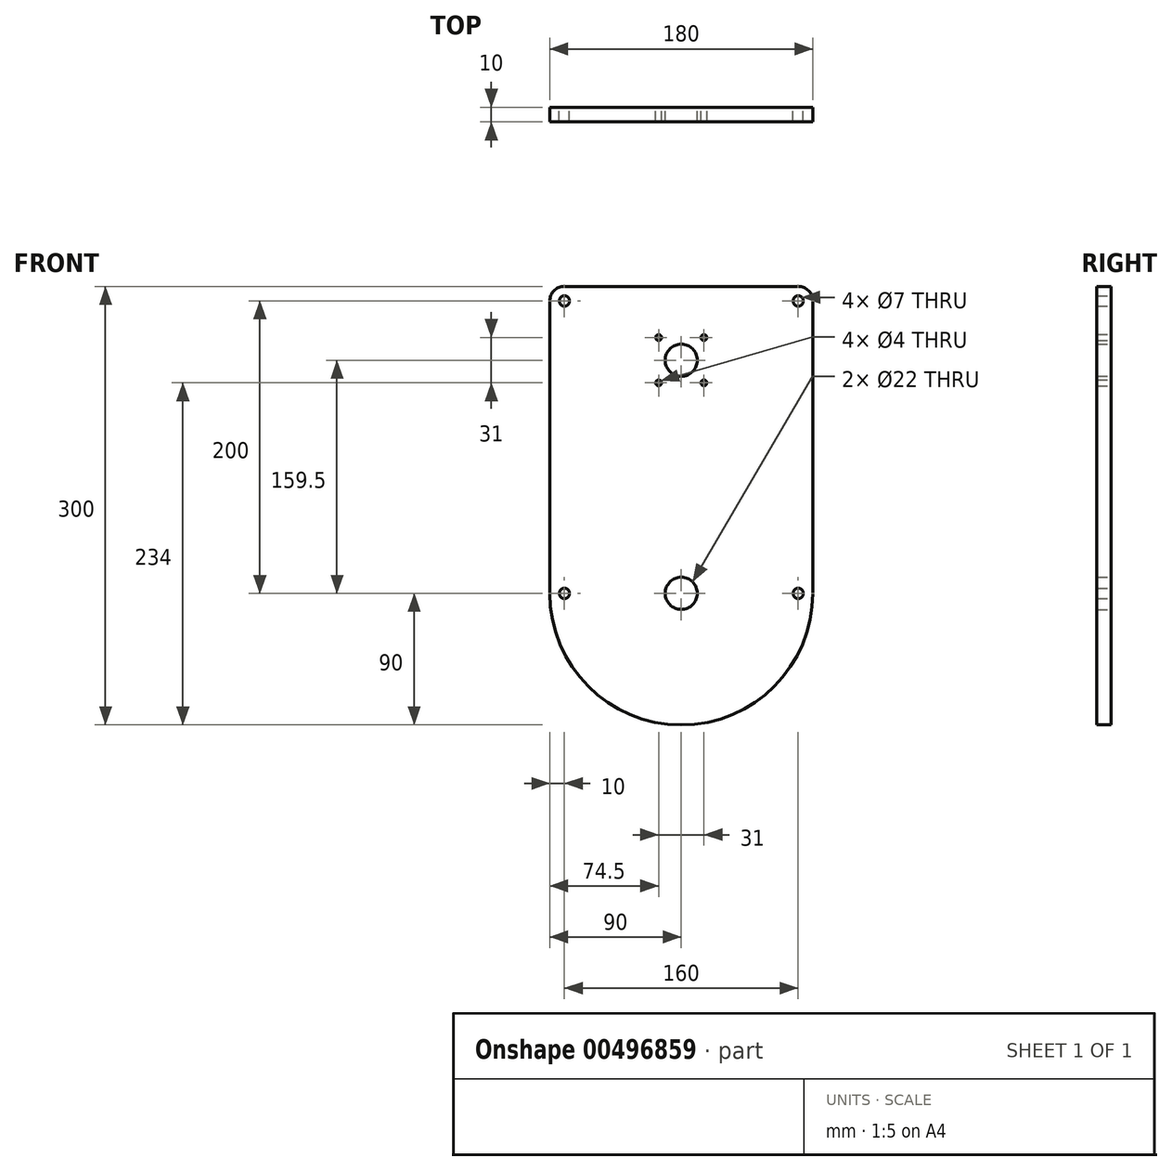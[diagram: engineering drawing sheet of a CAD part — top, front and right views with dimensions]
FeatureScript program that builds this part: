
annotation { "Feature Type Name" : "Feature", "Feature Type Description" : "" }
export const myFeature = defineFeature(function(context is Context, id is Id, definition is map)
    precondition{}
    {
        {
            var Q0;
            Q0=qCreatedBy(makeId("Front.planeOp"),FACE);
            var sketch = newSketch(context, id + "F0", { "sketchPlane" : qUnion([Q0])});
            skLineSegment(sketch, "E0.bottom", {"start": v(80, 150) * mm, "end": v(-80, 150) * mm});
            skLineSegment(sketch, "E0.top", {"start": v(0, -150) * mm, "end": v(0, -150) * mm});
            skLineSegment(sketch, "E0.left", {"start": v(90, 140) * mm, "end": v(90, -60) * mm});
            skLineSegment(sketch, "E0.right", {"start": v(-90, 140) * mm, "end": v(-90, -60) * mm});
            skPoint(sketch, "E0.middle", {"position": v(0, 0) * mm});
            skPoint(sketch, "E1.visualSharp", {"position": v(-90, 150) * mm});
            skArc(sketch, "E1.filletArc", {"start": v(-80, 150) * mm, "mid": v(-87.07, 147.07) * mm, "end": v(-90, 140) * mm});
            skPoint(sketch, "E2.visualSharp", {"position": v(90, 150) * mm});
            skArc(sketch, "E2.filletArc", {"start": v(90, 140) * mm, "mid": v(87.07, 147.07) * mm, "end": v(80, 150) * mm});
            skPoint(sketch, "E3.visualSharp", {"position": v(-90, -150) * mm});
            skArc(sketch, "E3.filletArc", {"start": v(-90, -60) * mm, "mid": v(-63.64, -123.64) * mm, "end": v(0, -150) * mm});
            skPoint(sketch, "E4.visualSharp", {"position": v(90, -150) * mm});
            skArc(sketch, "E4.filletArc", {"start": v(0, -150) * mm, "mid": v(63.64, -123.64) * mm, "end": v(90, -60) * mm});
            skCircle(sketch, "E5", {"center": v(0, -60) * mm, "radius": 11 * mm});
            skCircle(sketch, "E6", {"center": v(0, 99.5) * mm, "radius": 11 * mm});
            skCircle(sketch, "E7", {"center": v(-80, 140) * mm, "radius": 3.5 * mm});
            skCircle(sketch, "E8", {"center": v(80, 140) * mm, "radius": 3.5 * mm});
            skCircle(sketch, "E9", {"center": v(80, -60) * mm, "radius": 3.5 * mm});
            skCircle(sketch, "E10", {"center": v(-80, -60) * mm, "radius": 3.5 * mm});
            skCircle(sketch, "E11", {"center": v(-15.5, 115) * mm, "radius": 2 * mm});
            skCircle(sketch, "E12", {"center": v(15.5, 115) * mm, "radius": 2 * mm});
            skCircle(sketch, "E13", {"center": v(15.5, 84) * mm, "radius": 2 * mm});
            skCircle(sketch, "E14", {"center": v(-15.5, 84) * mm, "radius": 2 * mm});
            skSolve(sketch);
        }
        {
            var Q0;
            Q0=makeQuery(id+"F0.imprint","IMPRINT",FACE,{"disambiguationData":[TD([[makeQuery(id+"F0.imprint","IMPRINT",EDGE,{"derivedFrom":sQuery(id+"F0.wireOp",EDGE,"E0.bottom")}),1.0]])]});
            extrude(context, id + "F1", {"entities" : qUnion([Q0]), "depth" : 10 * mm, "offsetDistance" : 25 * mm});
        }
    });
